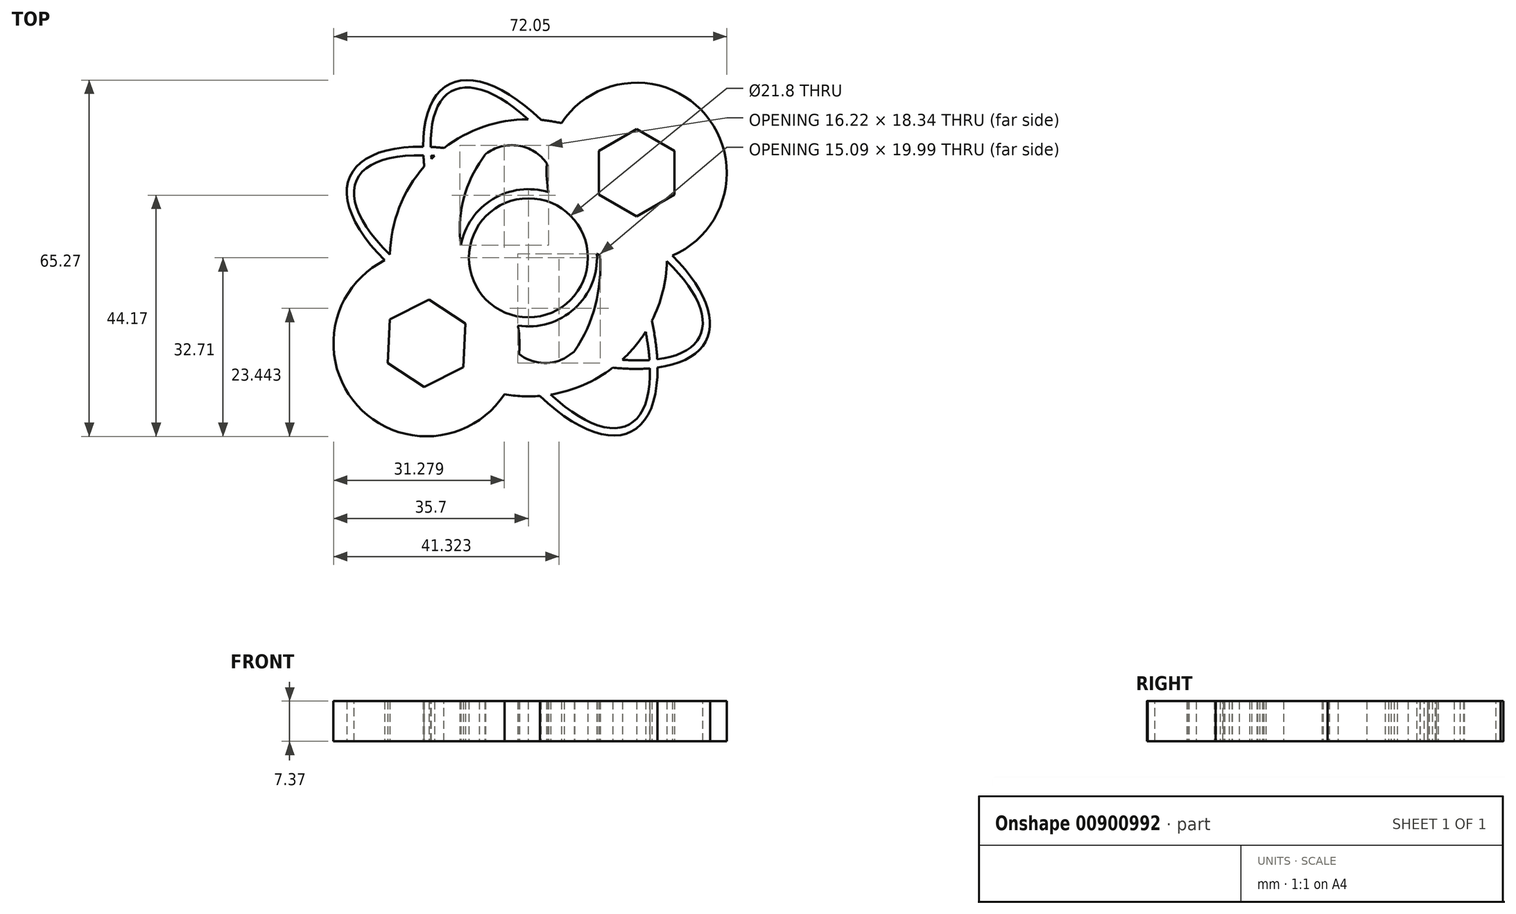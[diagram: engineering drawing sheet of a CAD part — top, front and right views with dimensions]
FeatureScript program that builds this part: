
annotation { "Feature Type Name" : "Feature", "Feature Type Description" : "" }
export const myFeature = defineFeature(function(context is Context, id is Id, definition is map)
    precondition{}
    {
        {
            var Q0;
            Q0=qCreatedBy(makeId("Top.planeOp"),FACE);
            var sketch = newSketch(context, id + "F0", { "sketchPlane" : qUnion([Q0])});
            skArc(sketch, "E0", {"start": v(6.03, 24.65) * mm, "mid": v(4.2, 25.03) * mm, "end": v(2.33, 25.27) * mm});
            skArc(sketch, "E1", {"start": v(-26.34, -0.45) * mm, "mid": v(-31.36, -27.03) * mm, "end": v(-4.4, -25) * mm});
            skArc(sketch, "E2", {"start": v(26.39, 0.4) * mm, "mid": v(32.48, 26.18) * mm, "end": v(6.03, 24.65) * mm});
            skArc(sketch, "E3", {"start": v(8.5, -17.08) * mm, "mid": v(12.25, -8.69) * mm, "end": v(13.1, 0.47) * mm});
            skArc(sketch, "E4", {"start": v(-7.82, 19.01) * mm, "mid": v(-7.9, 18.9) * mm, "end": v(-7.98, 18.8) * mm});
            skArc(sketch, "E5.trimOffspring", {"start": v(-4.4, -25) * mm, "mid": v(-1.16, -25.35) * mm, "end": v(2.09, -25.3) * mm});
            skArc(sketch, "E6", {"start": v(3.4, 17.29) * mm, "mid": v(-1.85, 20.55) * mm, "end": v(-7.82, 19.01) * mm});
            skArc(sketch, "E7", {"start": v(-1.73, -17.65) * mm, "mid": v(2.3, -19.23) * mm, "end": v(6.56, -18.44) * mm});
            skPoint(sketch, "E8.0.midPoint", {"position": v(12.34, 0.83) * mm});
            skPoint(sketch, "E9.orphan", {"position": v(0, 25.38) * mm});
            skPoint(sketch, "E10.orphan", {"position": v(0, -25.38) * mm});
            skArc(sketch, "E11.trimOffspring", {"start": v(-1.73, -17.65) * mm, "mid": v(-1.64, -16.71) * mm, "end": v(-1.61, -15.78) * mm});
            skArc(sketch, "E12.trimOffspring", {"start": v(3.4, 17.29) * mm, "mid": v(3.32, 16.2) * mm, "end": v(3.31, 15.1) * mm});
            skEllipticalArc(sketch, "E13", {});
            skEllipticalArc(sketch, "E14", {});
            skEllipticalArc(sketch, "E15", {});
            skEllipticalArc(sketch, "E16", {});
            skPoint(sketch, "E17.orphan", {"position": v(25.38, 0) * mm});
            skArc(sketch, "E18.trimOffspring", {"start": v(3.48, 13.17) * mm, "mid": v(3.58, 12.59) * mm, "end": v(3.7, 12.02) * mm});
            skArc(sketch, "E19.trimOffspring", {"start": v(-9.02, 17.32) * mm, "mid": v(-12.02, 10.1) * mm, "end": v(-12.36, 2.3) * mm});
            skEllipticalArc(sketch, "E20.trimOffspring", {});
            skEllipticalArc(sketch, "E21.trimOffspring", {});
            skEllipticalArc(sketch, "E22.trimOffspring", {});
            skEllipticalArc(sketch, "E23.trimOffspring", {});
            skEllipticalArc(sketch, "E24.trimOffspring", {});
            skEllipticalArc(sketch, "E25.trimOffspring", {});
            skEllipticalArc(sketch, "E26.trimOffspring", {});
            skEllipticalArc(sketch, "E27.trimOffspring", {});
            skEllipticalArc(sketch, "E28.trimOffspring", {});
            skArc(sketch, "E29.trimOffspring", {"start": v(-19.07, 16.75) * mm, "mid": v(-23.64, 9.23) * mm, "end": v(-25.37, 0.6) * mm});
            skPoint(sketch, "E30.orphan", {"position": v(-25.38, 0) * mm});
            skArc(sketch, "E31.trimOffspring", {"start": v(-1.7, -13.9) * mm, "mid": v(-1.8, -13.16) * mm, "end": v(-1.92, -12.42) * mm});
            skArc(sketch, "E32.trimOffspring", {"start": v(8.4, -17.17) * mm, "mid": v(8.45, -17.13) * mm, "end": v(8.5, -17.08) * mm});
            skEllipticalArc(sketch, "E33.trimOffspring", {});
            skEllipticalArc(sketch, "E34.trimOffspring", {});
            skArc(sketch, "E35.trimOffspring", {"start": v(0, 25.38) * mm, "mid": v(-8.17, 24.03) * mm, "end": v(-15.47, 20.12) * mm});
            skCircle(sketch, "E36", {"center": v(0, 0) * mm, "radius": 10.9 * mm});
            skArc(sketch, "E37.trimOffspring", {"start": v(12.55, 0.73) * mm, "mid": v(12.82, 0.6) * mm, "end": v(13.1, 0.47) * mm});
            skCircle(sketch, "E38.cCircle", {"center": v(-18.66, -15.66) * mm, "radius": 6.93 * mm, "construction": true});
            skLineSegment(sketch, "E38.0", {"start": v(-25.36, -11.3) * mm, "end": v(-18.23, -7.68) * mm});
            skLineSegment(sketch, "E38.1", {"start": v(-18.23, -7.68) * mm, "end": v(-11.53, -12.04) * mm});
            skLineSegment(sketch, "E38.2", {"start": v(-11.53, -12.04) * mm, "end": v(-11.95, -20.02) * mm});
            skLineSegment(sketch, "E38.3", {"start": v(-11.95, -20.02) * mm, "end": v(-19.08, -23.65) * mm});
            skLineSegment(sketch, "E38.4", {"start": v(-19.08, -23.65) * mm, "end": v(-25.78, -19.3) * mm});
            skLineSegment(sketch, "E38.5", {"start": v(-25.78, -19.3) * mm, "end": v(-25.36, -11.3) * mm});
            skPoint(sketch, "E38.0.midPoint", {"position": v(-21.8, -9.5) * mm});
            skArc(sketch, "E39", {"start": v(-1.92, -12.42) * mm, "mid": v(8.45, -9.3) * mm, "end": v(12.55, 0.73) * mm});
            skPoint(sketch, "E40.trimOffspring.end.orphan", {"position": v(-11.94, 0) * mm});
            skArc(sketch, "E41.trimOffspring", {"start": v(22.6, -11.53) * mm, "mid": v(24.6, -6.23) * mm, "end": v(25.37, -0.6) * mm});
            skEllipticalArc(sketch, "E42.trimOffspring", {});
            skLineSegment(sketch, "E43", {"start": v(8.4, -17.17) * mm, "end": v(6.56, -18.44) * mm});
            skLineSegment(sketch, "E44", {"start": v(-1.7, -13.9) * mm, "end": v(-1.61, -15.78) * mm});
            skArc(sketch, "E45.trimOffspring", {"start": v(17.2, -18.67) * mm, "mid": v(19.5, -16.24) * mm, "end": v(21.47, -13.54) * mm});
            skLineSegment(sketch, "E46", {"start": v(3.31, 15.1) * mm, "end": v(3.48, 13.17) * mm});
            skLineSegment(sketch, "E47", {"start": v(-7.98, 18.8) * mm, "end": v(-9.02, 17.32) * mm});
            skLineSegment(sketch, "E48", {"start": v(-17.2, 18.67) * mm, "end": v(-17.76, 18.13) * mm});
            skArc(sketch, "E49.trimOffspring", {"start": v(3.7, 12.02) * mm, "mid": v(-6.51, 10.75) * mm, "end": v(-12.36, 2.3) * mm});
            skArc(sketch, "E50.trimOffspring", {"start": v(4.1, -25.04) * mm, "mid": v(10.09, -23.29) * mm, "end": v(15.47, -20.12) * mm});
            skCircle(sketch, "E51.cCircle", {"center": v(19.83, 15.56) * mm, "radius": 6.93 * mm, "construction": true});
            skLineSegment(sketch, "E51.0", {"start": v(26.75, 19.56) * mm, "end": v(26.75, 11.56) * mm});
            skLineSegment(sketch, "E51.1", {"start": v(26.75, 11.56) * mm, "end": v(19.83, 7.56) * mm});
            skLineSegment(sketch, "E51.2", {"start": v(19.83, 7.56) * mm, "end": v(12.9, 11.56) * mm});
            skLineSegment(sketch, "E51.3", {"start": v(12.9, 11.56) * mm, "end": v(12.9, 19.56) * mm});
            skLineSegment(sketch, "E51.4", {"start": v(12.9, 19.56) * mm, "end": v(19.83, 23.56) * mm});
            skLineSegment(sketch, "E51.5", {"start": v(19.83, 23.56) * mm, "end": v(26.75, 19.56) * mm});
            skPoint(sketch, "E51.0.midPoint", {"position": v(26.75, 15.56) * mm});
            const initialGuessF0  = {"E13": [0, 0, -0.9090648193659409, 0.4166547181914174, 0.035925156480695566, 0.015170724476046038, 2.5530868606313226, 3.9874437217115872], "E14": [0.0021963788024957896, 0, 0.4661032836942935, -0.8847303142367153, 0.035925156480695566, 0.015170724476046038, 2.2403697164566196, 3.818377067565983], "E15": [0.002196378802495156, 0, -0.4679719654234763, 0.8837433109097284, 0.034596270940751364, 0.013449952857688843, 5.458644448078065, 0.6594801147061415], "E16": [0, 0, -0.9109490021903279, 0.4125189879368537, 0.03453192408295689, 0.01345824279481407, 2.5770942425936285, 3.969299482455225], "E20.trimOffspring": [0.002196378802495156, 0, -0.4679719654234763, 0.8837433109097284, 0.034596270940751364, 0.013449952857688843, 3.865835917245007, 4.060786830574715], "E21.trimOffspring": [0.0021963788024957896, 0, 0.4661032836942935, -0.8847303142367154, 0.035925156480695566, 0.015170724476046038, 0.744107371066988, 0.9898388859108965], "E22.trimOffspring": [0.002196378802495156, 0, -0.4679719654234763, 0.8837433109097284, 0.034596270940751364, 0.013449952857688843, 2.298952850129452, 3.803273970036519], "E23.trimOffspring": [0.0021963788024957896, 0, 0.4661032836942935, -0.8847303142367153, 0.035925156480695566, 0.015170724476046038, 5.382986248147139, 0.686346726572043], "E24.trimOffspring": [0, 0, -0.9090648193659409, 0.4166547181914174, 0.035925156480695566, 0.015170724476046038, 2.245596050030528, 2.4956246998336646], "E25.trimOffspring": [0.002196378802495156, 0, -0.4679719654234763, 0.8837433109097284, 0.034596270940751364, 0.013449952857688843, 0.7250017486088886, 0.7479864855769348], "E26.trimOffspring": [0.0021963788024957896, 0, 0.4661032836942935, -0.8847303142367154, 0.035925156480695566, 0.015170724476046038, 3.878743260070934, 3.9531757638445404], "E27.trimOffspring": [0, 0, -0.9090648193659409, 0.4166547181914174, 0.035925156480695566, 0.015170724476046038, 5.521212032251561, 0.8482914794487364], "E28.trimOffspring": [0, 0, -0.9109490021903279, 0.4125189879368537, 0.03453192408295689, 0.01345824279481407, 5.532832147103692, 0.8277068288654161], "E33.trimOffspring": [0, 0, -0.9109490021903279, 0.4125189879368537, 0.03453192408295689, 0.01345824279481407, 5.455478478314185, 5.478295967241081], "E34.trimOffspring": [0, 0, -0.9090648193659409, 0.4166547181914174, 0.035925156480695566, 0.015170724476046038, 5.387188703620321, 5.471115267117961], "E42.trimOffspring": [0, 0, -0.9109490021903279, 0.4125189879368537, 0.03453192408295689, 0.01345824279481407, 2.3138858247243923, 2.513814539736535]};
            skSetInitialGuess(sketch, initialGuessF0);
            skSolve(sketch);
        }
        {
            var Q0;
            {var subQ14=sQuery(id+"F0.wireOp",EDGE,"E13");var subQ30=makeQuery(id+"F0.imprint","INTERSECT",VERTEX,{"derivedFrom":[sQuery(id+"F0.wireOp",EDGE,"E2"),subQ14]});Q0=makeQuery(id+"F0.imprint","IMPRINT",FACE,{"disambiguationData":[TD([[makeQuery(id+"F0.imprint","IMPRINT",EDGE,{"disambiguationData":[TD([[subQ30,1.0]])],"derivedFrom":subQ14}),1.0]])]});}
            var Q1;
            {var subQ6=sQuery(id+"F0.wireOp",EDGE,"E4");Q1=makeQuery(id+"F0.imprint","IMPRINT",FACE,{"disambiguationData":[TD([[makeQuery(id+"F0.imprint","IMPRINT",EDGE,{"derivedFrom":subQ6}),-1.0]])]});}
            var Q2;
            {var subQ10=sQuery(id+"F0.wireOp",EDGE,"E19.trimOffspring");Q2=makeQuery(id+"F0.imprint","IMPRINT",FACE,{"disambiguationData":[TD([[makeQuery(id+"F0.imprint","IMPRINT",EDGE,{"derivedFrom":subQ10}),-1.0]])]});}
            var Q3;
            {var subQ3=sQuery(id+"F0.wireOp",EDGE,"E29.trimOffspring");Q3=makeQuery(id+"F0.imprint","IMPRINT",FACE,{"disambiguationData":[TD([[makeQuery(id+"F0.imprint","IMPRINT",EDGE,{"derivedFrom":subQ3}),1.0]])]});}
            var Q4;
            {var subQ1=sQuery(id+"F0.wireOp",EDGE,"E1");Q4=makeQuery(id+"F0.imprint","IMPRINT",FACE,{"disambiguationData":[TD([[makeQuery(id+"F0.imprint","IMPRINT",EDGE,{"derivedFrom":subQ1}),1.0]])]});}
            var Q5;
            {var subQ5=sQuery(id+"F0.wireOp",EDGE,"E7");Q5=makeQuery(id+"F0.imprint","IMPRINT",FACE,{"disambiguationData":[TD([[makeQuery(id+"F0.imprint","IMPRINT",EDGE,{"derivedFrom":subQ5}),-1.0]])]});}
            var Q6;
            Q6=makeQuery(id+"F0.imprint","IMPRINT",FACE,{"disambiguationData":[TD([[makeQuery(id+"F0.imprint","IMPRINT",EDGE,{"derivedFrom":sQuery(id+"F0.wireOp",EDGE,"E3")}),-1.0]])]});
            var Q7;
            {var subQ0=sQuery(id+"F0.wireOp",EDGE,"E16");var subQ1=sQuery(id+"F0.wireOp",EDGE,"E5.trimOffspring");var subQ2=makeQuery(id+"F0.imprint","INTERSECT",VERTEX,{"derivedFrom":[subQ1,subQ0]});Q7=makeQuery(id+"F0.imprint","IMPRINT",FACE,{"disambiguationData":[TD([[makeQuery(id+"F0.imprint","IMPRINT",EDGE,{"disambiguationData":[TD([[subQ2,1.0]])],"derivedFrom":subQ1}),1.0]])]});}
            var Q8;
            {var subQ4=sQuery(id+"F0.wireOp",EDGE,"E0");Q8=makeQuery(id+"F0.imprint","IMPRINT",FACE,{"disambiguationData":[TD([[makeQuery(id+"F0.imprint","IMPRINT",EDGE,{"derivedFrom":subQ4}),1.0]])]});}
            extrude(context, id + "F1", {"entities" : qUnion([Q0, Q1, Q2, Q3, Q4, Q5, Q6, Q7, Q8]), "depth" : 7.37 * mm, "offsetDistance" : 25.4 * mm});
        }
        {
            var Q0;
            Q0=makeQuery(id+"F0.imprint","IMPRINT",FACE,{"disambiguationData":[TD([[makeQuery(id+"F0.imprint","IMPRINT",EDGE,{"derivedFrom":sQuery(id+"F0.wireOp",EDGE,"E36")}),-1.0]])]});
            var Q1;
            Q1=makeQuery(id+"F0.imprint","IMPRINT",FACE,{"disambiguationData":[TD([[makeQuery(id+"F0.imprint","IMPRINT",EDGE,{"derivedFrom":sQuery(id+"F0.wireOp",EDGE,"E0")}),1.0]])]});
            extrude(context, id + "F2", {"entities" : qUnion([Q0, Q1]), "operationType" : NewBodyOperationType.ADD, "depth" : 7.3 * mm, "offsetDistance" : 25 * mm});
        }
    });
